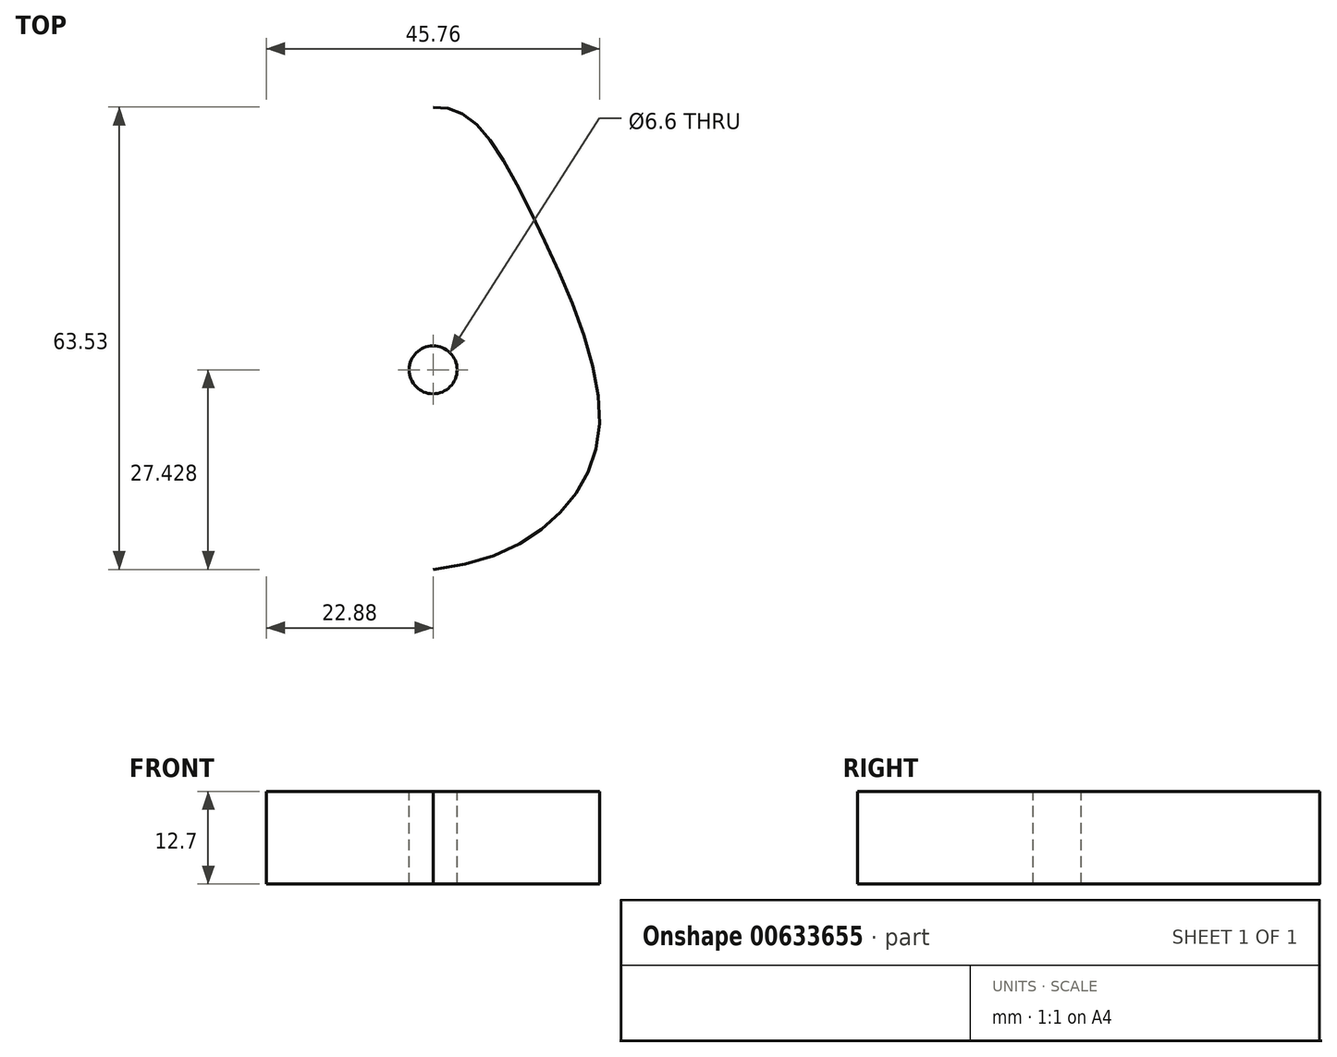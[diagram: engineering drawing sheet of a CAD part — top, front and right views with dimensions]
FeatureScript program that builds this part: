
annotation { "Feature Type Name" : "Feature", "Feature Type Description" : "" }
export const myFeature = defineFeature(function(context is Context, id is Id, definition is map)
    precondition{}
    {
        {
            var Q0;
            Q0=qCreatedBy(makeId("Top.planeOp"),FACE);
            var sketch = newSketch(context, id + "F0", { "sketchPlane" : qUnion([Q0])});
            skFitSpline(sketch, "E0", {"points": [v(0, 41.52) * mm, v(-5.6, 39.5) * mm, v(-14.51, 24.85) * mm, v(-22.86, 0) * mm, v(-17.67, -13.94) * mm, v(0, -21.98) * mm], "startDerivative": vector(-48.49, 3.99) * mm, "endDerivative": vector(106.83, -10.5) * mm});
            skLineSegment(sketch, "E1", {"start": v(0, 41.52) * mm, "end": v(0, -21.98) * mm, "construction": true});
            skFitSpline(sketch, "E2.MirrorCS", {"points": [v(0, 41.52) * mm, v(5.6, 39.5) * mm, v(14.51, 24.85) * mm, v(22.86, 0) * mm, v(17.67, -13.94) * mm, v(0, -21.98) * mm], "startDerivative": vector(48.49, 3.99) * mm, "endDerivative": vector(-106.83, -10.5) * mm});
            skSolve(sketch);
        }
        {
            var Q0;
            Q0 = qSketchRegion(id + "F0", true);
            extrude(context, id + "F1", {"entities" : qUnion([Q0]), "depth" : 12.7 * mm, "offsetDistance" : 25.4 * mm});
        }
        {
            var Q0;
            Q0=makeQuery(id+"F1.opExtrude","CAP_FACE",FACE,{"disambiguationData":[OSD([sQuery(id+"F0.wireOp",EDGE,"E0"),sQuery(id+"F0.wireOp",EDGE,"E2.MirrorCS")])],"isStart":false});
            var sketch = newSketch(context, id + "F2", { "sketchPlane" : qUnion([Q0])});
            skCircle(sketch, "E3", {"center": v(0, 5.45) * mm, "radius": 3.3 * mm});
            skSolve(sketch);
        }
        {
            var Q0;
            Q0 = qSketchRegion(id + "F2", true);
            extrude(context, id + "F3", {"entities" : qUnion([Q0]), "operationType" : NewBodyOperationType.REMOVE, "oppositeDirection" : true, "depth" : 12.7 * mm, "offsetDistance" : 25.4 * mm});
        }
    });
